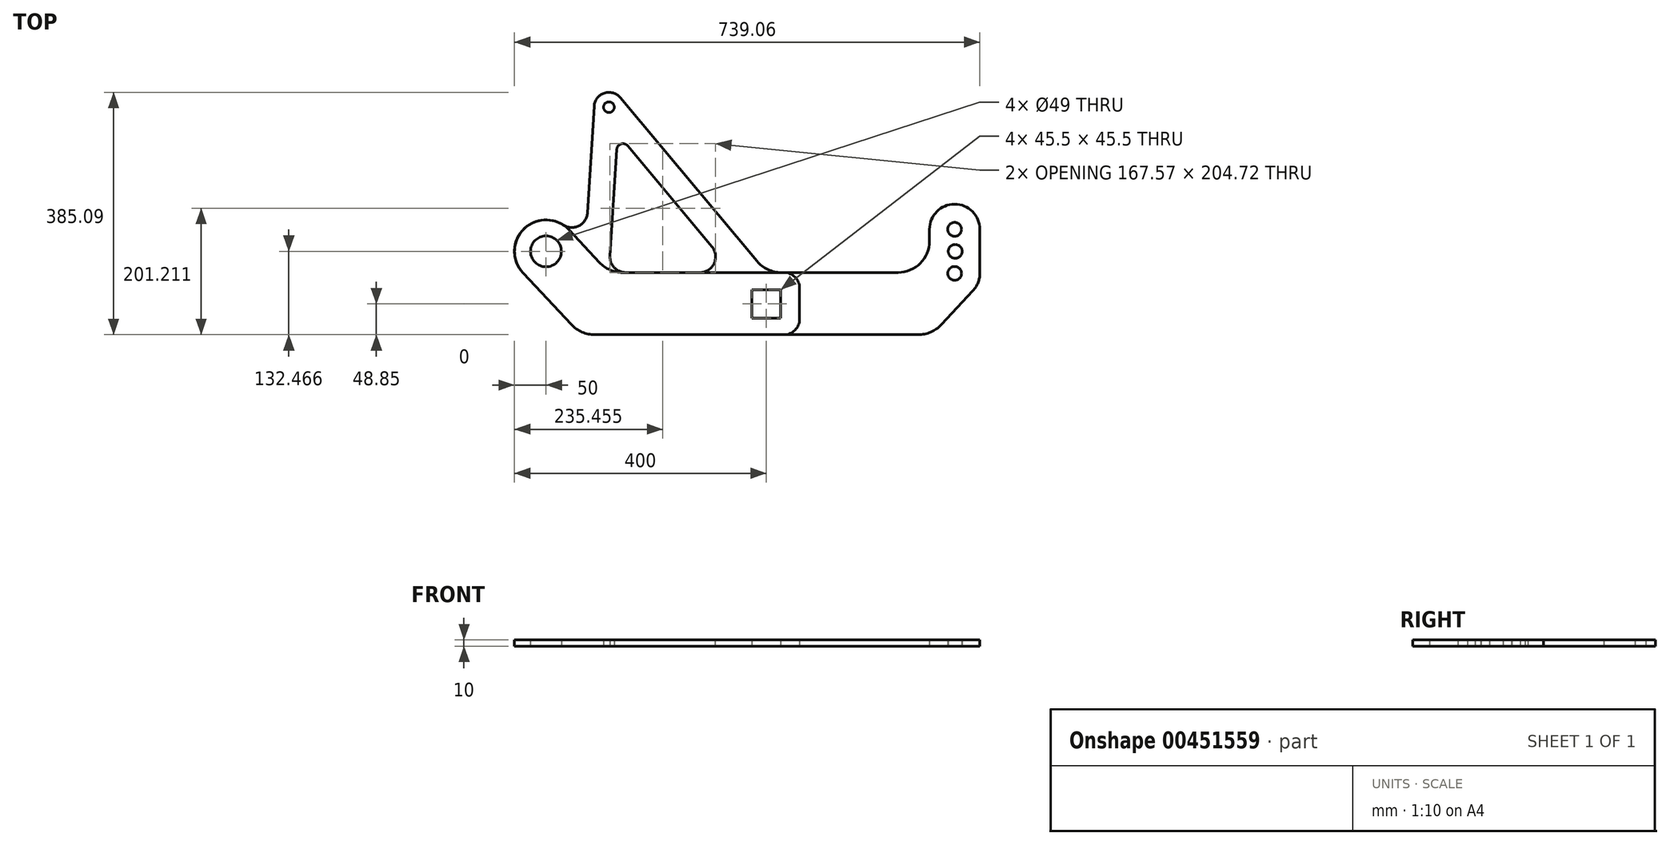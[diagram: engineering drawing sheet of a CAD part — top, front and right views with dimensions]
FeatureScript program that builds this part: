
annotation { "Feature Type Name" : "Feature", "Feature Type Description" : "" }
export const myFeature = defineFeature(function(context is Context, id is Id, definition is map)
    precondition{}
    {
        {
            var Q0;
            Q0=qCreatedBy(makeId("Top.planeOp"),FACE);
            var sketch = newSketch(context, id + "F0", { "sketchPlane" : qUnion([Q0])});
            skLineSegment(sketch, "E0", {"start": v(-365.7, -365) * mm, "end": v(634.3, -365) * mm});
            skLineSegment(sketch, "E1.bottom", {"start": v(-22.75, 22.75) * mm, "end": v(22.75, 22.75) * mm});
            skLineSegment(sketch, "E1.top", {"start": v(-22.75, -22.75) * mm, "end": v(22.75, -22.75) * mm});
            skLineSegment(sketch, "E1.left", {"start": v(-22.75, 22.75) * mm, "end": v(-22.75, -22.75) * mm});
            skLineSegment(sketch, "E1.right", {"start": v(22.75, 22.75) * mm, "end": v(22.75, -22.75) * mm});
            skCircle(sketch, "E2", {"center": v(-350, 83.62) * mm, "radius": 24.5 * mm});
            skCircle(sketch, "E3", {"center": v(-350, 83.62) * mm, "radius": 50 * mm});
            skLineSegment(sketch, "E4", {"start": v(-150, -253.28) * mm, "end": v(-150, 446.72) * mm});
            skLineSegment(sketch, "E5", {"start": v(0, 22.75) * mm, "end": v(0, -22.75) * mm});
            skLineSegment(sketch, "E6", {"start": v(-22.75, 0) * mm, "end": v(22.75, 0) * mm});
            skCircle(sketch, "E7", {"center": v(-350, 83.62) * mm, "radius": 31.5 * mm});
            skCircle(sketch, "E8", {"center": v(0, 0) * mm, "radius": 50 * mm});
            skLineSegment(sketch, "E9", {"start": v(0, 50) * mm, "end": v(-250, 50) * mm});
            skLineSegment(sketch, "E10", {"start": v(-10.66, -48.85) * mm, "end": v(262.86, -48.85) * mm});
            skLineSegment(sketch, "E11", {"start": v(-250, 50) * mm, "end": v(-313.5, 117.8) * mm});
            skLineSegment(sketch, "E12", {"start": v(-294.42, -48.85) * mm, "end": v(-386.5, 49.43) * mm});
            skLineSegment(sketch, "E13", {"start": v(-294.42, -48.85) * mm, "end": v(-10.66, -48.85) * mm});
            skCircle(sketch, "E14", {"center": v(300, 83.62) * mm, "radius": 11 * mm});
            skLineSegment(sketch, "E15", {"start": v(0, 50) * mm, "end": v(303.46, 50) * mm});
            skCircle(sketch, "E16", {"center": v(299.06, 118.62) * mm, "radius": 11 * mm});
            skCircle(sketch, "E17", {"center": v(299.06, 48.62) * mm, "radius": 11 * mm});
            skCircle(sketch, "E18", {"center": v(299.06, 118.62) * mm, "radius": 40 * mm});
            skCircle(sketch, "E19", {"center": v(299.06, 48.62) * mm, "radius": 40 * mm});
            skLineSegment(sketch, "E20", {"start": v(262.86, -48.85) * mm, "end": v(328.31, 21.34) * mm});
            skLineSegment(sketch, "E21", {"start": v(339.06, 118.62) * mm, "end": v(339.06, 48.62) * mm});
            skLineSegment(sketch, "E22", {"start": v(259.06, 83.62) * mm, "end": v(259.06, 118.62) * mm});
            skLineSegment(sketch, "E23", {"start": v(259.06, 83.62) * mm, "end": v(259.06, 50) * mm});
            skLineSegment(sketch, "E24", {"start": v(52.75, 50) * mm, "end": v(52.75, -48.85) * mm});
            skCircle(sketch, "E25", {"center": v(-250, 312.74) * mm, "radius": 8.5 * mm});
            skCircle(sketch, "E26", {"center": v(-250, 312.74) * mm, "radius": 23.5 * mm});
            skCircle(sketch, "E27", {"center": v(-250, 312.74) * mm, "radius": 75 * mm});
            skLineSegment(sketch, "E28", {"start": v(-231.96, 327.8) * mm, "end": v(0, 50) * mm});
            skLineSegment(sketch, "E29", {"start": v(-251.94, 289.33) * mm, "end": v(-52.11, 50) * mm});
            skLineSegment(sketch, "E30", {"start": v(-234.58, 295) * mm, "end": v(-250, 50) * mm});
            skLineSegment(sketch, "E31", {"start": v(-273.45, 314.22) * mm, "end": v(-287.56, 90.1) * mm});
            skSolve(sketch);
        }
        {
            var Q0;
            {var subQ10=sQuery(id+"F0.wireOp",EDGE,"E12");Q0=makeQuery(id+"F0.imprint","IMPRINT",FACE,{"disambiguationData":[TD([[makeQuery(id+"F0.imprint","IMPRINT",EDGE,{"derivedFrom":subQ10}),-1.0]])]});}
            var Q1;
            {var subQ2=sQuery(id+"F0.wireOp",EDGE,"E4");var subQ6=sQuery(id+"F0.wireOp",EDGE,"E13");var subQ7=makeQuery(id+"F0.imprint","INTERSECT",VERTEX,{"derivedFrom":[subQ2,subQ6]});Q1=makeQuery(id+"F0.imprint","IMPRINT",FACE,{"disambiguationData":[TD([[makeQuery(id+"F0.imprint","IMPRINT",EDGE,{"disambiguationData":[TD([[subQ7,-1.0]])],"derivedFrom":subQ2}),-1.0]])]});}
            var Q2;
            {var subQ10=sQuery(id+"F0.wireOp",EDGE,"E1.bottom");var subQ12=sQuery(id+"F0.wireOp",EDGE,"E1.left");var subQ15=makeQuery(id+"F0.imprint","INTERSECT",VERTEX,{"derivedFrom":[subQ10,subQ12]});Q2=makeQuery(id+"F0.imprint","IMPRINT",FACE,{"disambiguationData":[TD([[makeQuery(id+"F0.imprint","IMPRINT",EDGE,{"disambiguationData":[TD([[subQ15,-1.0]])],"derivedFrom":subQ10}),1.0]])]});}
            var Q3;
            {var subQ5=sQuery(id+"F0.wireOp",EDGE,"E24");Q3=makeQuery(id+"F0.imprint","IMPRINT",FACE,{"disambiguationData":[TD([[makeQuery(id+"F0.imprint","IMPRINT",EDGE,{"derivedFrom":subQ5}),-1.0]])]});}
            var Q4;
            Q4=makeQuery(id+"F0.imprint","IMPRINT",FACE,{"disambiguationData":[TD([[makeQuery(id+"F0.imprint","IMPRINT",EDGE,{"derivedFrom":sQuery(id+"F0.wireOp",EDGE,"E7")}),-1.0]])]});
            var Q5;
            Q5=makeQuery(id+"F0.imprint","IMPRINT",FACE,{"disambiguationData":[TD([[makeQuery(id+"F0.imprint","IMPRINT",EDGE,{"derivedFrom":sQuery(id+"F0.wireOp",EDGE,"E2")}),-1.0]])]});
            extrude(context, id + "F1", {"entities" : qUnion([Q0, Q1, Q2, Q3, Q4, Q5]), "depth" : 10 * mm, "offsetDistance" : 25 * mm});
        }
        {
            var Q0;
            Q0=makeQuery(id+"F1.opExtrude","SWEPT_EDGE",EDGE,{"disambiguationData":[OSD([sQuery(id+"F0.wireOp",EDGE,"E12"),sQuery(id+"F0.wireOp",EDGE,"E13")])]});
            var Q1;
            Q1=makeQuery(id+"F1.opExtrude","SWEPT_EDGE",EDGE,{"disambiguationData":[OSD([sQuery(id+"F0.wireOp",EDGE,"E9"),sQuery(id+"F0.wireOp",EDGE,"E11"),sQuery(id+"F0.wireOp",EDGE,"E30")])]});
            fillet(context, id + "F2", {"entities" : qUnion([Q0, Q1]), "radius" : 50 * mm, "tangentPropagation" : true, "allowEdgeOverflow" : false});
        }
        {
            var Q0;
            Q0=makeQuery(id+"F1.opExtrude","SWEPT_EDGE",EDGE,{"disambiguationData":[OSD([sQuery(id+"F0.wireOp",EDGE,"E15"),sQuery(id+"F0.wireOp",EDGE,"E24")])]});
            var Q1;
            Q1=makeQuery(id+"F1.opExtrude","SWEPT_EDGE",EDGE,{"disambiguationData":[OSD([sQuery(id+"F0.wireOp",EDGE,"E10"),sQuery(id+"F0.wireOp",EDGE,"E24")])]});
            fillet(context, id + "F3", {"entities" : qUnion([Q0, Q1]), "radius" : 25 * mm, "tangentPropagation" : true, "allowEdgeOverflow" : false});
        }
        {
            var Q0;
            Q0=makeQuery(id+"F0.imprint","IMPRINT",FACE,{"disambiguationData":[TD([[makeQuery(id+"F0.imprint","IMPRINT",EDGE,{"derivedFrom":sQuery(id+"F0.wireOp",EDGE,"E7")}),-1.0]])]});
            var Q1;
            Q1=makeQuery(id+"F0.imprint","IMPRINT",FACE,{"disambiguationData":[TD([[makeQuery(id+"F0.imprint","IMPRINT",EDGE,{"derivedFrom":sQuery(id+"F0.wireOp",EDGE,"E2")}),-1.0]])]});
            var Q2;
            {var subQ10=sQuery(id+"F0.wireOp",EDGE,"E12");Q2=makeQuery(id+"F0.imprint","IMPRINT",FACE,{"disambiguationData":[TD([[makeQuery(id+"F0.imprint","IMPRINT",EDGE,{"derivedFrom":subQ10}),-1.0]])]});}
            var Q3;
            {var subQ2=sQuery(id+"F0.wireOp",EDGE,"E4");var subQ6=sQuery(id+"F0.wireOp",EDGE,"E13");var subQ7=makeQuery(id+"F0.imprint","INTERSECT",VERTEX,{"derivedFrom":[subQ2,subQ6]});Q3=makeQuery(id+"F0.imprint","IMPRINT",FACE,{"disambiguationData":[TD([[makeQuery(id+"F0.imprint","IMPRINT",EDGE,{"disambiguationData":[TD([[subQ7,-1.0]])],"derivedFrom":subQ2}),-1.0]])]});}
            var Q4;
            {var subQ10=sQuery(id+"F0.wireOp",EDGE,"E1.bottom");var subQ12=sQuery(id+"F0.wireOp",EDGE,"E1.left");var subQ15=makeQuery(id+"F0.imprint","INTERSECT",VERTEX,{"derivedFrom":[subQ10,subQ12]});Q4=makeQuery(id+"F0.imprint","IMPRINT",FACE,{"disambiguationData":[TD([[makeQuery(id+"F0.imprint","IMPRINT",EDGE,{"disambiguationData":[TD([[subQ15,-1.0]])],"derivedFrom":subQ10}),1.0]])]});}
            var Q5;
            {var subQ5=sQuery(id+"F0.wireOp",EDGE,"E24");Q5=makeQuery(id+"F0.imprint","IMPRINT",FACE,{"disambiguationData":[TD([[makeQuery(id+"F0.imprint","IMPRINT",EDGE,{"derivedFrom":subQ5}),-1.0]])]});}
            var Q6;
            {var subQ4=sQuery(id+"F0.wireOp",EDGE,"E20");Q6=makeQuery(id+"F0.imprint","IMPRINT",FACE,{"disambiguationData":[TD([[makeQuery(id+"F0.imprint","IMPRINT",EDGE,{"derivedFrom":subQ4}),1.0]])]});}
            var Q7;
            Q7=makeQuery(id+"F0.imprint","IMPRINT",FACE,{"disambiguationData":[TD([[makeQuery(id+"F0.imprint","IMPRINT",EDGE,{"derivedFrom":sQuery(id+"F0.wireOp",EDGE,"E17")}),-1.0]])]});
            var Q8;
            {var subQ0=sQuery(id+"F0.wireOp",EDGE,"E21");Q8=makeQuery(id+"F0.imprint","IMPRINT",FACE,{"disambiguationData":[TD([[makeQuery(id+"F0.imprint","IMPRINT",EDGE,{"derivedFrom":subQ0}),-1.0]])]});}
            var Q9;
            {var subQ0=sQuery(id+"F0.wireOp",EDGE,"E22");Q9=makeQuery(id+"F0.imprint","IMPRINT",FACE,{"disambiguationData":[TD([[makeQuery(id+"F0.imprint","IMPRINT",EDGE,{"derivedFrom":subQ0}),-1.0]])]});}
            var Q10;
            Q10=makeQuery(id+"F0.imprint","IMPRINT",FACE,{"disambiguationData":[TD([[makeQuery(id+"F0.imprint","IMPRINT",EDGE,{"derivedFrom":sQuery(id+"F0.wireOp",EDGE,"E16")}),-1.0]])]});
            var Q11;
            {var subQ0=sQuery(id+"F0.wireOp",EDGE,"E19");var subQ1=sQuery(id+"F0.wireOp",EDGE,"E14");var subQ2=makeQuery(id+"F0.imprint","INTERSECT",VERTEX,{"disambiguationData":[OD(0.0)],"derivedFrom":[subQ1,subQ0]});Q11=makeQuery(id+"F0.imprint","IMPRINT",FACE,{"disambiguationData":[TD([[makeQuery(id+"F0.imprint","IMPRINT",EDGE,{"disambiguationData":[TD([[subQ2,-1.0]])],"derivedFrom":subQ1}),-1.0]])]});}
            var Q12;
            {var subQ0=sQuery(id+"F0.wireOp",EDGE,"E19");var subQ1=sQuery(id+"F0.wireOp",EDGE,"E14");var subQ2=makeQuery(id+"F0.imprint","INTERSECT",VERTEX,{"disambiguationData":[OD(1.0)],"derivedFrom":[subQ1,subQ0]});Q12=makeQuery(id+"F0.imprint","IMPRINT",FACE,{"disambiguationData":[TD([[makeQuery(id+"F0.imprint","IMPRINT",EDGE,{"disambiguationData":[TD([[subQ2,1.0]])],"derivedFrom":subQ1}),-1.0]])]});}
            extrude(context, id + "F4", {"entities" : qUnion([Q0, Q1, Q2, Q3, Q4, Q5, Q6, Q7, Q8, Q9, Q10, Q11, Q12]), "depth" : 10 * mm, "offsetDistance" : 25 * mm});
        }
        {
            var Q0;
            Q0=makeQuery(id+"F4.opExtrude","SWEPT_EDGE",EDGE,{"disambiguationData":[OSD([sQuery(id+"F0.wireOp",EDGE,"E12"),sQuery(id+"F0.wireOp",EDGE,"E13")])]});
            var Q1;
            Q1=makeQuery(id+"F4.opExtrude","SWEPT_EDGE",EDGE,{"disambiguationData":[OSD([sQuery(id+"F0.wireOp",EDGE,"E10"),sQuery(id+"F0.wireOp",EDGE,"E20")])]});
            var Q2;
            Q2=makeQuery(id+"F4.opExtrude","SWEPT_EDGE",EDGE,{"disambiguationData":[OSD([sQuery(id+"F0.wireOp",EDGE,"E15"),sQuery(id+"F0.wireOp",EDGE,"E23")])]});
            var Q3;
            Q3=makeQuery(id+"F4.opExtrude","SWEPT_EDGE",EDGE,{"disambiguationData":[OSD([sQuery(id+"F0.wireOp",EDGE,"E9"),sQuery(id+"F0.wireOp",EDGE,"E11"),sQuery(id+"F0.wireOp",EDGE,"E30")])]});
            fillet(context, id + "F5", {"entities" : qUnion([Q0, Q1, Q2, Q3]), "radius" : 50 * mm, "tangentPropagation" : true, "allowEdgeOverflow" : false});
        }
        {
            var Q0;
            {var subQ10=sQuery(id+"F0.wireOp",EDGE,"E12");Q0=makeQuery(id+"F0.imprint","IMPRINT",FACE,{"disambiguationData":[TD([[makeQuery(id+"F0.imprint","IMPRINT",EDGE,{"derivedFrom":subQ10}),-1.0]])]});}
            var Q1;
            Q1=makeQuery(id+"F0.imprint","IMPRINT",FACE,{"disambiguationData":[TD([[makeQuery(id+"F0.imprint","IMPRINT",EDGE,{"derivedFrom":sQuery(id+"F0.wireOp",EDGE,"E7")}),-1.0]])]});
            var Q2;
            Q2=makeQuery(id+"F0.imprint","IMPRINT",FACE,{"disambiguationData":[TD([[makeQuery(id+"F0.imprint","IMPRINT",EDGE,{"derivedFrom":sQuery(id+"F0.wireOp",EDGE,"E2")}),-1.0]])]});
            var Q3;
            {var subQ2=sQuery(id+"F0.wireOp",EDGE,"E4");var subQ6=sQuery(id+"F0.wireOp",EDGE,"E13");var subQ7=makeQuery(id+"F0.imprint","INTERSECT",VERTEX,{"derivedFrom":[subQ2,subQ6]});Q3=makeQuery(id+"F0.imprint","IMPRINT",FACE,{"disambiguationData":[TD([[makeQuery(id+"F0.imprint","IMPRINT",EDGE,{"disambiguationData":[TD([[subQ7,-1.0]])],"derivedFrom":subQ2}),-1.0]])]});}
            var Q4;
            {var subQ10=sQuery(id+"F0.wireOp",EDGE,"E1.bottom");var subQ12=sQuery(id+"F0.wireOp",EDGE,"E1.left");var subQ15=makeQuery(id+"F0.imprint","INTERSECT",VERTEX,{"derivedFrom":[subQ10,subQ12]});Q4=makeQuery(id+"F0.imprint","IMPRINT",FACE,{"disambiguationData":[TD([[makeQuery(id+"F0.imprint","IMPRINT",EDGE,{"disambiguationData":[TD([[subQ15,-1.0]])],"derivedFrom":subQ10}),1.0]])]});}
            var Q5;
            {var subQ4=sQuery(id+"F0.wireOp",EDGE,"E20");Q5=makeQuery(id+"F0.imprint","IMPRINT",FACE,{"disambiguationData":[TD([[makeQuery(id+"F0.imprint","IMPRINT",EDGE,{"derivedFrom":subQ4}),1.0]])]});}
            var Q6;
            {var subQ5=sQuery(id+"F0.wireOp",EDGE,"E24");Q6=makeQuery(id+"F0.imprint","IMPRINT",FACE,{"disambiguationData":[TD([[makeQuery(id+"F0.imprint","IMPRINT",EDGE,{"derivedFrom":subQ5}),-1.0]])]});}
            var Q7;
            Q7=makeQuery(id+"F0.imprint","IMPRINT",FACE,{"disambiguationData":[TD([[makeQuery(id+"F0.imprint","IMPRINT",EDGE,{"derivedFrom":sQuery(id+"F0.wireOp",EDGE,"E17")}),-1.0]])]});
            var Q8;
            {var subQ0=sQuery(id+"F0.wireOp",EDGE,"E22");Q8=makeQuery(id+"F0.imprint","IMPRINT",FACE,{"disambiguationData":[TD([[makeQuery(id+"F0.imprint","IMPRINT",EDGE,{"derivedFrom":subQ0}),-1.0]])]});}
            var Q9;
            {var subQ0=sQuery(id+"F0.wireOp",EDGE,"E21");Q9=makeQuery(id+"F0.imprint","IMPRINT",FACE,{"disambiguationData":[TD([[makeQuery(id+"F0.imprint","IMPRINT",EDGE,{"derivedFrom":subQ0}),-1.0]])]});}
            var Q10;
            Q10=makeQuery(id+"F0.imprint","IMPRINT",FACE,{"disambiguationData":[TD([[makeQuery(id+"F0.imprint","IMPRINT",EDGE,{"derivedFrom":sQuery(id+"F0.wireOp",EDGE,"E16")}),-1.0]])]});
            var Q11;
            {var subQ0=sQuery(id+"F0.wireOp",EDGE,"E19");var subQ1=sQuery(id+"F0.wireOp",EDGE,"E14");var subQ2=makeQuery(id+"F0.imprint","INTERSECT",VERTEX,{"disambiguationData":[OD(1.0)],"derivedFrom":[subQ1,subQ0]});Q11=makeQuery(id+"F0.imprint","IMPRINT",FACE,{"disambiguationData":[TD([[makeQuery(id+"F0.imprint","IMPRINT",EDGE,{"disambiguationData":[TD([[subQ2,1.0]])],"derivedFrom":subQ1}),-1.0]])]});}
            var Q12;
            {var subQ0=sQuery(id+"F0.wireOp",EDGE,"E19");var subQ1=sQuery(id+"F0.wireOp",EDGE,"E14");var subQ2=makeQuery(id+"F0.imprint","INTERSECT",VERTEX,{"disambiguationData":[OD(0.0)],"derivedFrom":[subQ1,subQ0]});Q12=makeQuery(id+"F0.imprint","IMPRINT",FACE,{"disambiguationData":[TD([[makeQuery(id+"F0.imprint","IMPRINT",EDGE,{"disambiguationData":[TD([[subQ2,-1.0]])],"derivedFrom":subQ1}),-1.0]])]});}
            var Q13;
            {var subQ0=sQuery(id+"F0.wireOp",EDGE,"E28");var subQ1=sQuery(id+"F0.wireOp",EDGE,"E4");var subQ2=makeQuery(id+"F0.imprint","INTERSECT",VERTEX,{"derivedFrom":[subQ1,subQ0]});Q13=makeQuery(id+"F0.imprint","IMPRINT",FACE,{"disambiguationData":[TD([[makeQuery(id+"F0.imprint","IMPRINT",EDGE,{"disambiguationData":[TD([[subQ2,1.0]])],"derivedFrom":subQ1}),1.0]])]});}
            var Q14;
            {var subQ0=sQuery(id+"F0.wireOp",EDGE,"E28");var subQ1=sQuery(id+"F0.wireOp",EDGE,"E4");var subQ2=makeQuery(id+"F0.imprint","INTERSECT",VERTEX,{"derivedFrom":[subQ1,subQ0]});Q14=makeQuery(id+"F0.imprint","IMPRINT",FACE,{"disambiguationData":[TD([[makeQuery(id+"F0.imprint","IMPRINT",EDGE,{"disambiguationData":[TD([[subQ2,1.0]])],"derivedFrom":subQ1}),-1.0]])]});}
            var Q15;
            {var subQ3=sQuery(id+"F0.wireOp",EDGE,"E31");var subQ5=sQuery(id+"F0.wireOp",EDGE,"E27");var subQ6=makeQuery(id+"F0.imprint","INTERSECT",VERTEX,{"derivedFrom":[subQ5,subQ3]});Q15=makeQuery(id+"F0.imprint","IMPRINT",FACE,{"disambiguationData":[TD([[makeQuery(id+"F0.imprint","IMPRINT",EDGE,{"disambiguationData":[TD([[subQ6,-1.0]])],"derivedFrom":subQ5}),-1.0]])]});}
            var Q16;
            {var subQ0=sQuery(id+"F0.wireOp",EDGE,"E30");var subQ1=sQuery(id+"F0.wireOp",EDGE,"E26");var subQ2=makeQuery(id+"F0.imprint","INTERSECT",VERTEX,{"derivedFrom":[subQ1,subQ0]});Q16=makeQuery(id+"F0.imprint","IMPRINT",FACE,{"disambiguationData":[TD([[makeQuery(id+"F0.imprint","IMPRINT",EDGE,{"disambiguationData":[TD([[subQ2,1.0]])],"derivedFrom":subQ1}),-1.0]])]});}
            var Q17;
            {var subQ0=sQuery(id+"F0.wireOp",EDGE,"E28");var subQ1=sQuery(id+"F0.wireOp",EDGE,"E26");var subQ2=makeQuery(id+"F0.imprint","INTERSECT",VERTEX,{"derivedFrom":[subQ1,subQ0]});Q17=makeQuery(id+"F0.imprint","IMPRINT",FACE,{"disambiguationData":[TD([[makeQuery(id+"F0.imprint","IMPRINT",EDGE,{"disambiguationData":[TD([[subQ2,1.0]])],"derivedFrom":subQ1}),-1.0]])]});}
            var Q18;
            Q18=makeQuery(id+"F0.imprint","IMPRINT",FACE,{"disambiguationData":[TD([[makeQuery(id+"F0.imprint","IMPRINT",EDGE,{"derivedFrom":sQuery(id+"F0.wireOp",EDGE,"E25")}),-1.0]])]});
            var Q19;
            {var subQ0=sQuery(id+"F0.wireOp",EDGE,"E29");var subQ1=sQuery(id+"F0.wireOp",EDGE,"E26");var subQ2=makeQuery(id+"F0.imprint","INTERSECT",VERTEX,{"derivedFrom":[subQ1,subQ0]});Q19=makeQuery(id+"F0.imprint","IMPRINT",FACE,{"disambiguationData":[TD([[makeQuery(id+"F0.imprint","IMPRINT",EDGE,{"disambiguationData":[TD([[subQ2,1.0]])],"derivedFrom":subQ1}),-1.0]])]});}
            extrude(context, id + "F6", {"entities" : qUnion([Q0, Q1, Q2, Q3, Q4, Q5, Q6, Q7, Q8, Q9, Q10, Q11, Q12, Q13, Q14, Q15, Q16, Q17, Q18, Q19]), "depth" : 10 * mm, "offsetDistance" : 25 * mm});
        }
        {
            var Q0;
            Q0=makeQuery(id+"F6.opExtrude","SWEPT_EDGE",EDGE,{"disambiguationData":[OSD([sQuery(id+"F0.wireOp",EDGE,"E12"),sQuery(id+"F0.wireOp",EDGE,"E13")])]});
            var Q1;
            Q1=makeQuery(id+"F6.opExtrude","SWEPT_EDGE",EDGE,{"disambiguationData":[OSD([sQuery(id+"F0.wireOp",EDGE,"E10"),sQuery(id+"F0.wireOp",EDGE,"E20")])]});
            var Q2;
            Q2=makeQuery(id+"F6.opExtrude","SWEPT_EDGE",EDGE,{"disambiguationData":[OSD([sQuery(id+"F0.wireOp",EDGE,"E15"),sQuery(id+"F0.wireOp",EDGE,"E23")])]});
            var Q3;
            Q3=makeQuery(id+"F6.opExtrude","SWEPT_EDGE",EDGE,{"disambiguationData":[OSD([sQuery(id+"F0.wireOp",EDGE,"E8"),sQuery(id+"F0.wireOp",EDGE,"E9"),sQuery(id+"F0.wireOp",EDGE,"E15"),sQuery(id+"F0.wireOp",EDGE,"E28")])]});
            fillet(context, id + "F7", {"entities" : qUnion([Q0, Q1, Q2, Q3]), "radius" : 50 * mm, "tangentPropagation" : true, "allowEdgeOverflow" : false});
        }
        {
            var Q0;
            Q0=makeQuery(id+"F6.opExtrude","SWEPT_EDGE",EDGE,{"disambiguationData":[OSD([sQuery(id+"F0.wireOp",EDGE,"E9"),sQuery(id+"F0.wireOp",EDGE,"E29")])]});
            var Q1;
            Q1=makeQuery(id+"F6.opExtrude","SWEPT_EDGE",EDGE,{"disambiguationData":[OSD([sQuery(id+"F0.wireOp",EDGE,"E9"),sQuery(id+"F0.wireOp",EDGE,"E11"),sQuery(id+"F0.wireOp",EDGE,"E30")])]});
            var Q2;
            Q2=makeQuery(id+"F6.opExtrude","SWEPT_EDGE",EDGE,{"disambiguationData":[OSD([sQuery(id+"F0.wireOp",EDGE,"E11"),sQuery(id+"F0.wireOp",EDGE,"E31")])]});
            fillet(context, id + "F8", {"entities" : qUnion([Q0, Q1, Q2]), "radius" : 25 * mm, "tangentPropagation" : true, "allowEdgeOverflow" : false});
        }
        {
            var Q0;
            Q0=makeQuery(id+"F6.opExtrude","SWEPT_EDGE",EDGE,{"disambiguationData":[OSD([sQuery(id+"F0.wireOp",EDGE,"E27"),sQuery(id+"F0.wireOp",EDGE,"E29")])]});
            var Q1;
            Q1=makeQuery(id+"F6.opExtrude","SWEPT_EDGE",EDGE,{"disambiguationData":[OSD([sQuery(id+"F0.wireOp",EDGE,"E27"),sQuery(id+"F0.wireOp",EDGE,"E30")])]});
            fillet(context, id + "F9", {"entities" : qUnion([Q0, Q1]), "radius" : 10 * mm, "tangentPropagation" : true, "allowEdgeOverflow" : false});
        }
        {
            var Q0;
            {var subQ10=sQuery(id+"F0.wireOp",EDGE,"E12");Q0=makeQuery(id+"F0.imprint","IMPRINT",FACE,{"disambiguationData":[TD([[makeQuery(id+"F0.imprint","IMPRINT",EDGE,{"derivedFrom":subQ10}),-1.0]])]});}
            var Q1;
            Q1=makeQuery(id+"F0.imprint","IMPRINT",FACE,{"disambiguationData":[TD([[makeQuery(id+"F0.imprint","IMPRINT",EDGE,{"derivedFrom":sQuery(id+"F0.wireOp",EDGE,"E7")}),-1.0]])]});
            var Q2;
            Q2=makeQuery(id+"F0.imprint","IMPRINT",FACE,{"disambiguationData":[TD([[makeQuery(id+"F0.imprint","IMPRINT",EDGE,{"derivedFrom":sQuery(id+"F0.wireOp",EDGE,"E2")}),-1.0]])]});
            var Q3;
            {var subQ2=sQuery(id+"F0.wireOp",EDGE,"E4");var subQ6=sQuery(id+"F0.wireOp",EDGE,"E13");var subQ7=makeQuery(id+"F0.imprint","INTERSECT",VERTEX,{"derivedFrom":[subQ2,subQ6]});Q3=makeQuery(id+"F0.imprint","IMPRINT",FACE,{"disambiguationData":[TD([[makeQuery(id+"F0.imprint","IMPRINT",EDGE,{"disambiguationData":[TD([[subQ7,-1.0]])],"derivedFrom":subQ2}),-1.0]])]});}
            var Q4;
            {var subQ10=sQuery(id+"F0.wireOp",EDGE,"E1.bottom");var subQ12=sQuery(id+"F0.wireOp",EDGE,"E1.left");var subQ15=makeQuery(id+"F0.imprint","INTERSECT",VERTEX,{"derivedFrom":[subQ10,subQ12]});Q4=makeQuery(id+"F0.imprint","IMPRINT",FACE,{"disambiguationData":[TD([[makeQuery(id+"F0.imprint","IMPRINT",EDGE,{"disambiguationData":[TD([[subQ15,-1.0]])],"derivedFrom":subQ10}),1.0]])]});}
            var Q5;
            {var subQ5=sQuery(id+"F0.wireOp",EDGE,"E24");Q5=makeQuery(id+"F0.imprint","IMPRINT",FACE,{"disambiguationData":[TD([[makeQuery(id+"F0.imprint","IMPRINT",EDGE,{"derivedFrom":subQ5}),-1.0]])]});}
            var Q6;
            {var subQ0=sQuery(id+"F0.wireOp",EDGE,"E28");var subQ1=sQuery(id+"F0.wireOp",EDGE,"E4");var subQ2=makeQuery(id+"F0.imprint","INTERSECT",VERTEX,{"derivedFrom":[subQ1,subQ0]});Q6=makeQuery(id+"F0.imprint","IMPRINT",FACE,{"disambiguationData":[TD([[makeQuery(id+"F0.imprint","IMPRINT",EDGE,{"disambiguationData":[TD([[subQ2,1.0]])],"derivedFrom":subQ1}),-1.0]])]});}
            var Q7;
            {var subQ0=sQuery(id+"F0.wireOp",EDGE,"E28");var subQ1=sQuery(id+"F0.wireOp",EDGE,"E4");var subQ2=makeQuery(id+"F0.imprint","INTERSECT",VERTEX,{"derivedFrom":[subQ1,subQ0]});Q7=makeQuery(id+"F0.imprint","IMPRINT",FACE,{"disambiguationData":[TD([[makeQuery(id+"F0.imprint","IMPRINT",EDGE,{"disambiguationData":[TD([[subQ2,1.0]])],"derivedFrom":subQ1}),1.0]])]});}
            var Q8;
            {var subQ3=sQuery(id+"F0.wireOp",EDGE,"E31");var subQ5=sQuery(id+"F0.wireOp",EDGE,"E27");var subQ6=makeQuery(id+"F0.imprint","INTERSECT",VERTEX,{"derivedFrom":[subQ5,subQ3]});Q8=makeQuery(id+"F0.imprint","IMPRINT",FACE,{"disambiguationData":[TD([[makeQuery(id+"F0.imprint","IMPRINT",EDGE,{"disambiguationData":[TD([[subQ6,-1.0]])],"derivedFrom":subQ5}),-1.0]])]});}
            var Q9;
            {var subQ0=sQuery(id+"F0.wireOp",EDGE,"E29");var subQ1=sQuery(id+"F0.wireOp",EDGE,"E26");var subQ2=makeQuery(id+"F0.imprint","INTERSECT",VERTEX,{"derivedFrom":[subQ1,subQ0]});Q9=makeQuery(id+"F0.imprint","IMPRINT",FACE,{"disambiguationData":[TD([[makeQuery(id+"F0.imprint","IMPRINT",EDGE,{"disambiguationData":[TD([[subQ2,1.0]])],"derivedFrom":subQ1}),-1.0]])]});}
            var Q10;
            {var subQ0=sQuery(id+"F0.wireOp",EDGE,"E28");var subQ1=sQuery(id+"F0.wireOp",EDGE,"E26");var subQ2=makeQuery(id+"F0.imprint","INTERSECT",VERTEX,{"derivedFrom":[subQ1,subQ0]});Q10=makeQuery(id+"F0.imprint","IMPRINT",FACE,{"disambiguationData":[TD([[makeQuery(id+"F0.imprint","IMPRINT",EDGE,{"disambiguationData":[TD([[subQ2,1.0]])],"derivedFrom":subQ1}),-1.0]])]});}
            var Q11;
            {var subQ0=sQuery(id+"F0.wireOp",EDGE,"E30");var subQ1=sQuery(id+"F0.wireOp",EDGE,"E26");var subQ2=makeQuery(id+"F0.imprint","INTERSECT",VERTEX,{"derivedFrom":[subQ1,subQ0]});Q11=makeQuery(id+"F0.imprint","IMPRINT",FACE,{"disambiguationData":[TD([[makeQuery(id+"F0.imprint","IMPRINT",EDGE,{"disambiguationData":[TD([[subQ2,1.0]])],"derivedFrom":subQ1}),-1.0]])]});}
            var Q12;
            Q12=makeQuery(id+"F0.imprint","IMPRINT",FACE,{"disambiguationData":[TD([[makeQuery(id+"F0.imprint","IMPRINT",EDGE,{"derivedFrom":sQuery(id+"F0.wireOp",EDGE,"E25")}),-1.0]])]});
            extrude(context, id + "F10", {"entities" : qUnion([Q0, Q1, Q2, Q3, Q4, Q5, Q6, Q7, Q8, Q9, Q10, Q11, Q12]), "depth" : 10 * mm, "offsetDistance" : 25 * mm});
        }
        {
            var Q0;
            Q0=makeQuery(id+"F10.opExtrude","SWEPT_EDGE",EDGE,{"disambiguationData":[OSD([sQuery(id+"F0.wireOp",EDGE,"E12"),sQuery(id+"F0.wireOp",EDGE,"E13")])]});
            var Q1;
            Q1=makeQuery(id+"F10.opExtrude","SWEPT_EDGE",EDGE,{"disambiguationData":[OSD([sQuery(id+"F0.wireOp",EDGE,"E8"),sQuery(id+"F0.wireOp",EDGE,"E9"),sQuery(id+"F0.wireOp",EDGE,"E15"),sQuery(id+"F0.wireOp",EDGE,"E28")])]});
            fillet(context, id + "F11", {"entities" : qUnion([Q0, Q1]), "radius" : 50 * mm, "tangentPropagation" : true, "allowEdgeOverflow" : false});
        }
        {
            var Q0;
            Q0=makeQuery(id+"F10.opExtrude","SWEPT_EDGE",EDGE,{"disambiguationData":[OSD([sQuery(id+"F0.wireOp",EDGE,"E15"),sQuery(id+"F0.wireOp",EDGE,"E24")])]});
            var Q1;
            Q1=makeQuery(id+"F10.opExtrude","SWEPT_EDGE",EDGE,{"disambiguationData":[OSD([sQuery(id+"F0.wireOp",EDGE,"E10"),sQuery(id+"F0.wireOp",EDGE,"E24")])]});
            var Q2;
            Q2=makeQuery(id+"F10.opExtrude","SWEPT_EDGE",EDGE,{"disambiguationData":[OSD([sQuery(id+"F0.wireOp",EDGE,"E11"),sQuery(id+"F0.wireOp",EDGE,"E31")])]});
            var Q3;
            Q3=makeQuery(id+"F10.opExtrude","SWEPT_EDGE",EDGE,{"disambiguationData":[OSD([sQuery(id+"F0.wireOp",EDGE,"E9"),sQuery(id+"F0.wireOp",EDGE,"E29")])]});
            var Q4;
            Q4=makeQuery(id+"F10.opExtrude","SWEPT_EDGE",EDGE,{"disambiguationData":[OSD([sQuery(id+"F0.wireOp",EDGE,"E9"),sQuery(id+"F0.wireOp",EDGE,"E11"),sQuery(id+"F0.wireOp",EDGE,"E30")])]});
            fillet(context, id + "F12", {"entities" : qUnion([Q0, Q1, Q2, Q3, Q4]), "radius" : 25 * mm, "tangentPropagation" : true, "allowEdgeOverflow" : false});
        }
        {
            var Q0;
            Q0=makeQuery(id+"F10.opExtrude","SWEPT_EDGE",EDGE,{"disambiguationData":[OSD([sQuery(id+"F0.wireOp",EDGE,"E27"),sQuery(id+"F0.wireOp",EDGE,"E29")])]});
            var Q1;
            Q1=makeQuery(id+"F10.opExtrude","SWEPT_EDGE",EDGE,{"disambiguationData":[OSD([sQuery(id+"F0.wireOp",EDGE,"E27"),sQuery(id+"F0.wireOp",EDGE,"E30")])]});
            fillet(context, id + "F13", {"entities" : qUnion([Q0, Q1]), "radius" : 10 * mm, "tangentPropagation" : true, "allowEdgeOverflow" : false});
        }
    });
